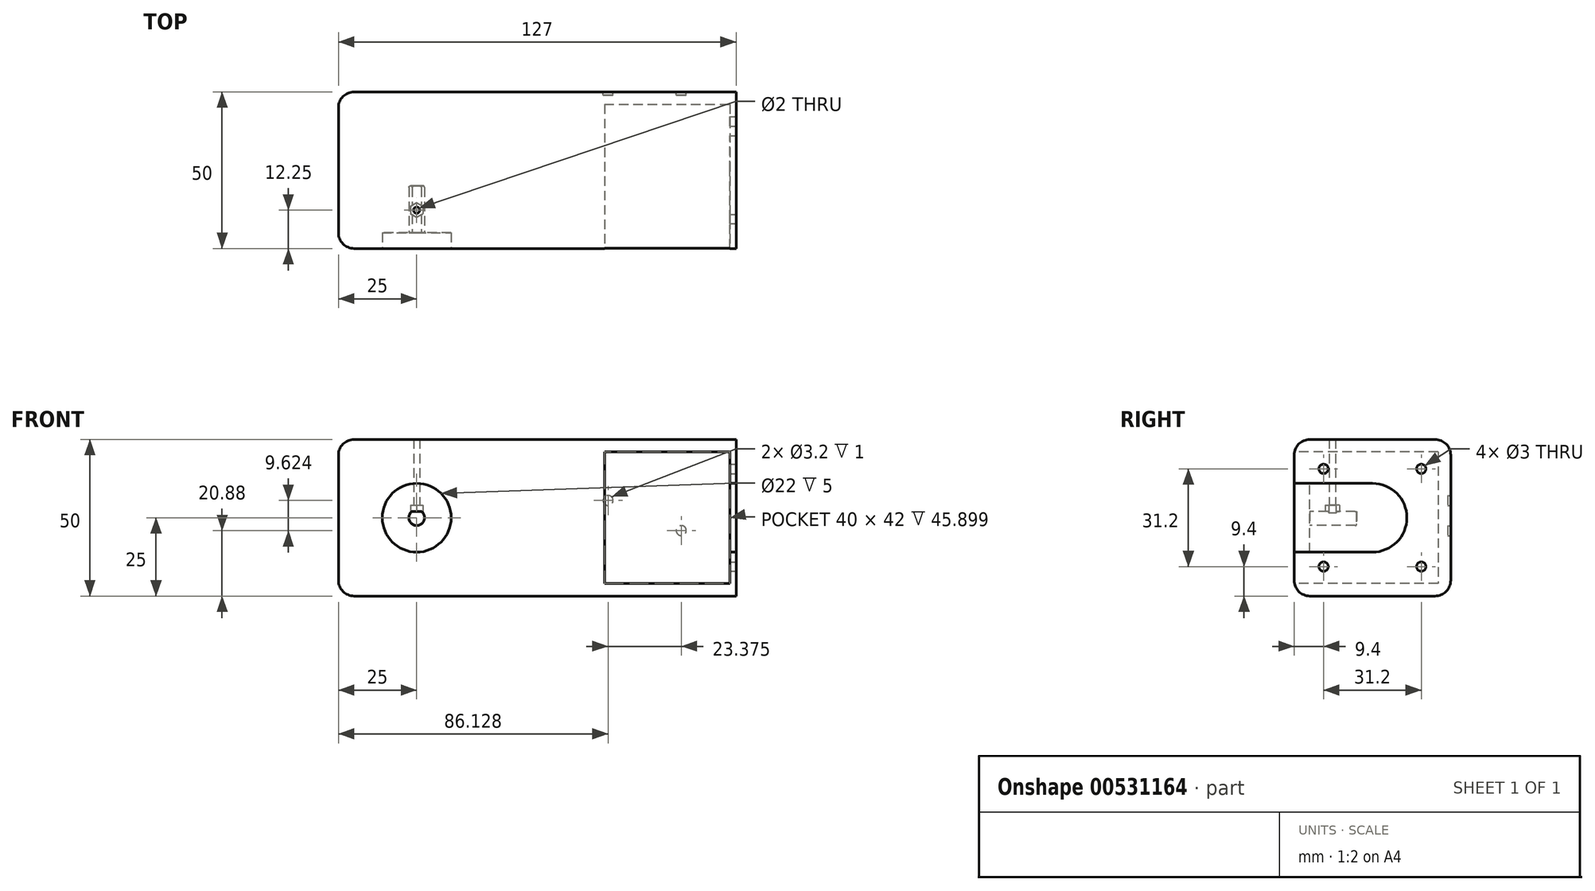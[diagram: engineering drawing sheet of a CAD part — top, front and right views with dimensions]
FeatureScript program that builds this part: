
annotation { "Feature Type Name" : "Feature", "Feature Type Description" : "" }
export const myFeature = defineFeature(function(context is Context, id is Id, definition is map)
    precondition{}
    {
        {
            var Q0;
            Q0=qCreatedBy(makeId("Front.planeOp"),FACE);
            var sketch = newSketch(context, id + "F0", { "sketchPlane" : qUnion([Q0])});
            skLineSegment(sketch, "E0.bottom", {"start": v(63.5, -25) * mm, "end": v(-63.5, -25) * mm});
            skLineSegment(sketch, "E0.top", {"start": v(63.5, 25) * mm, "end": v(-63.5, 25) * mm});
            skLineSegment(sketch, "E0.left", {"start": v(63.5, -25) * mm, "end": v(63.5, 25) * mm});
            skLineSegment(sketch, "E0.right", {"start": v(-63.5, -25) * mm, "end": v(-63.5, 25) * mm});
            skPoint(sketch, "E0.middle", {"position": v(0, 0) * mm});
            skSolve(sketch);
        }
        {
            var Q0;
            Q0 = qSketchRegion(id + "F0", true);
            extrude(context, id + "F1", {"entities" : qUnion([Q0]), "depth" : 50 * mm, "offsetDistance" : 25 * mm});
        }
        {
            var Q0;
            Q0=makeQuery(id+"F1.opExtrude","SWEPT_FACE",FACE,{"disambiguationData":[OSD([sQuery(id+"F0.wireOp",EDGE,"E0.left")])]});
            var sketch = newSketch(context, id + "F2", { "sketchPlane" : qUnion([Q0])});
            skLineSegment(sketch, "E1", {"start": v(-46, 16.76) * mm, "end": v(-41.76, 21) * mm});
            skLineSegment(sketch, "E2", {"start": v(-41.76, 21) * mm, "end": v(-8.24, 21) * mm});
            skLineSegment(sketch, "E3", {"start": v(-8.24, 21) * mm, "end": v(-4, 16.76) * mm});
            skLineSegment(sketch, "E4", {"start": v(-4, 16.76) * mm, "end": v(-4, -16.76) * mm});
            skLineSegment(sketch, "E5", {"start": v(-4, -16.76) * mm, "end": v(-8.24, -21) * mm});
            skLineSegment(sketch, "E6", {"start": v(-8.24, -21) * mm, "end": v(-41.76, -21) * mm});
            skLineSegment(sketch, "E7", {"start": v(-41.76, -21) * mm, "end": v(-46, -16.76) * mm});
            skLineSegment(sketch, "E8", {"start": v(-46, -16.76) * mm, "end": v(-46, 16.76) * mm});
            skLineSegment(sketch, "E9", {"start": v(-25, 21) * mm, "end": v(-25, 25) * mm, "construction": true});
            skLineSegment(sketch, "E10", {"start": v(-25, -21) * mm, "end": v(-25, -25) * mm, "construction": true});
            skLineSegment(sketch, "E11", {"start": v(-46, 0) * mm, "end": v(-50, 0) * mm, "construction": true});
            skLineSegment(sketch, "E12", {"start": v(0, 0) * mm, "end": v(-4, 0) * mm, "construction": true});
            skSolve(sketch);
        }
        {
            var Q0;
            Q0 = qSketchRegion(id + "F2", true);
            extrude(context, id + "F3", {"entities" : qUnion([Q0]), "operationType" : NewBodyOperationType.REMOVE, "oppositeDirection" : true, "depth" : 42 * mm, "offsetDistance" : 25 * mm});
        }
        {
            var Q0;
            Q0=makeQuery(id+"F1.opExtrude","CAP_FACE",FACE,{"disambiguationData":[OSD([sQuery(id+"F0.wireOp",EDGE,"E0.bottom"),sQuery(id+"F0.wireOp",EDGE,"E0.top"),sQuery(id+"F0.wireOp",EDGE,"E0.left"),sQuery(id+"F0.wireOp",EDGE,"E0.right")])],"isStart":false});
            var sketch = newSketch(context, id + "F4", { "sketchPlane" : qUnion([Q0])});
            skCircle(sketch, "E13", {"center": v(-38.5, 0) * mm, "radius": 11 * mm});
            skSolve(sketch);
        }
        {
            var Q0;
            Q0 = qSketchRegion(id + "F4", true);
            extrude(context, id + "F5", {"entities" : qUnion([Q0]), "operationType" : NewBodyOperationType.REMOVE, "oppositeDirection" : true, "depth" : 5 * mm, "offsetDistance" : 25 * mm});
        }
        {
            var Q0;
            Q0=makeQuery(id+"F5.boolean.opBoolean","COPY",FACE,{"derivedFrom":makeQuery(id+"F5.opExtrude","CAP_FACE",FACE,{"disambiguationData":[OSD([sQuery(id+"F4.wireOp",EDGE,"E13")])],"isStart":false})});
            var sketch = newSketch(context, id + "F6", { "sketchPlane" : qUnion([Q0])});
            skArc(sketch, "E14", {"start": v(-40, 2) * mm, "mid": v(-38.5, -2.5) * mm, "end": v(-37, 2) * mm});
            skLineSegment(sketch, "E15", {"start": v(-40, 2) * mm, "end": v(-37, 2) * mm});
            skSolve(sketch);
        }
        {
            var Q0;
            Q0 = qSketchRegion(id + "F6", true);
            extrude(context, id + "F7", {"entities" : qUnion([Q0]), "operationType" : NewBodyOperationType.REMOVE, "oppositeDirection" : true, "depth" : 15 * mm, "offsetDistance" : 25 * mm});
        }
        {
            var Q0;
            Q0=makeQuery(id+"F7.boolean.opBoolean","COPY",EDGE,{"derivedFrom":makeQuery(id+"F7.opExtrude","CAP_EDGE",EDGE,{"disambiguationData":[OSD([sQuery(id+"F6.wireOp",EDGE,"E14")])],"isStart":false})});
            fillet(context, id + "F8", {"entities" : qUnion([Q0]), "radius" : .5 * mm, "tangentPropagation" : true, "allowEdgeOverflow" : false});
        }
        {
            var Q0;
            Q0=makeQuery(id+"F1.opExtrude","CAP_EDGE",EDGE,{"disambiguationData":[OSD([sQuery(id+"F0.wireOp",EDGE,"E0.top")])],"isStart":false});
            var Q1;
            Q1=makeQuery(id+"F1.opExtrude","CAP_EDGE",EDGE,{"disambiguationData":[OSD([sQuery(id+"F0.wireOp",EDGE,"E0.bottom")])],"isStart":false});
            var Q2;
            Q2=makeQuery(id+"F1.opExtrude","CAP_EDGE",EDGE,{"disambiguationData":[OSD([sQuery(id+"F0.wireOp",EDGE,"E0.top")])],"isStart":true});
            var Q3;
            Q3=makeQuery(id+"F1.opExtrude","CAP_EDGE",EDGE,{"disambiguationData":[OSD([sQuery(id+"F0.wireOp",EDGE,"E0.bottom")])],"isStart":true});
            var Q4;
            Q4=makeQuery(id+"F1.opExtrude","SWEPT_EDGE",EDGE,{"disambiguationData":[OSD([sQuery(id+"F0.wireOp",EDGE,"E0.top"),sQuery(id+"F0.wireOp",EDGE,"E0.right")])]});
            var Q5;
            Q5=makeQuery(id+"F1.opExtrude","SWEPT_EDGE",EDGE,{"disambiguationData":[OSD([sQuery(id+"F0.wireOp",EDGE,"E0.bottom"),sQuery(id+"F0.wireOp",EDGE,"E0.right")])]});
            var Q6;
            Q6=makeQuery(id+"F1.opExtrude","CAP_EDGE",EDGE,{"disambiguationData":[OSD([sQuery(id+"F0.wireOp",EDGE,"E0.right")])],"isStart":true});
            var Q7;
            Q7=makeQuery(id+"F1.opExtrude","CAP_EDGE",EDGE,{"disambiguationData":[OSD([sQuery(id+"F0.wireOp",EDGE,"E0.right")])],"isStart":false});
            fillet(context, id + "F9", {"entities" : qUnion([Q0, Q1, Q2, Q3, Q4, Q5, Q6, Q7]), "radius" : 5 * mm, "tangentPropagation" : true, "allowEdgeOverflow" : false});
        }
        {
            var Q0;
            Q0=makeQuery(id+"F1.opExtrude","SWEPT_FACE",FACE,{"disambiguationData":[OSD([sQuery(id+"F0.wireOp",EDGE,"E0.left")])]});
            var sketch = newSketch(context, id + "F10", { "sketchPlane" : qUnion([Q0])});
            skPoint(sketch, "E16.middle", {"position": v(-25, 0) * mm});
            skLineSegment(sketch, "E17", {"start": v(-46, -16.76) * mm, "end": v(-41.76, -21) * mm});
            skLineSegment(sketch, "E18", {"start": v(-46, -16.76) * mm, "end": v(-46, 16.76) * mm});
            skLineSegment(sketch, "E19", {"start": v(-46, 16.76) * mm, "end": v(-41.76, 21) * mm});
            skLineSegment(sketch, "E20", {"start": v(-41.76, -21) * mm, "end": v(-8.24, -21) * mm});
            skLineSegment(sketch, "E21", {"start": v(-8.24, -21) * mm, "end": v(-4, -16.76) * mm});
            skLineSegment(sketch, "E22", {"start": v(-4, -16.76) * mm, "end": v(-4, 16.76) * mm});
            skLineSegment(sketch, "E23", {"start": v(-4, 16.76) * mm, "end": v(-8.24, 21) * mm});
            skLineSegment(sketch, "E24", {"start": v(-8.24, 21) * mm, "end": v(-41.76, 21) * mm});
            skLineSegment(sketch, "E25", {"start": v(-25, 0) * mm, "end": v(-4, 0) * mm, "construction": true});
            skLineSegment(sketch, "E26", {"start": v(-25, 0) * mm, "end": v(-25, 21) * mm, "construction": true});
            skLineSegment(sketch, "E27", {"start": v(-25, 0) * mm, "end": v(-25, -21) * mm, "construction": true});
            skLineSegment(sketch, "E28", {"start": v(-25, 0) * mm, "end": v(-46, 0) * mm, "construction": true});
            skLineSegment(sketch, "E29.bottom", {"start": v(-9.4, -15.6) * mm, "end": v(-40.6, -15.6) * mm});
            skLineSegment(sketch, "E29.top", {"start": v(-9.4, 15.6) * mm, "end": v(-40.6, 15.6) * mm});
            skLineSegment(sketch, "E29.left", {"start": v(-9.4, -15.6) * mm, "end": v(-9.4, 15.6) * mm});
            skLineSegment(sketch, "E29.right", {"start": v(-40.6, -15.6) * mm, "end": v(-40.6, 15.6) * mm});
            skCircle(sketch, "E30", {"center": v(-40.6, 15.6) * mm, "radius": 1.5 * mm});
            skCircle(sketch, "E31", {"center": v(-9.4, 15.6) * mm, "radius": 1.5 * mm});
            skCircle(sketch, "E32", {"center": v(-9.4, -15.6) * mm, "radius": 1.5 * mm});
            skCircle(sketch, "E33", {"center": v(-40.6, -15.6) * mm, "radius": 1.5 * mm});
            skLineSegment(sketch, "E34.bottom", {"start": v(-33.1, 21) * mm, "end": v(-16.9, 21) * mm});
            skLineSegment(sketch, "E35", {"start": v(-16.9, 21) * mm, "end": v(-8.24, 21) * mm, "construction": true});
            skLineSegment(sketch, "E36", {"start": v(-33.1, 21) * mm, "end": v(-41.76, 21) * mm, "construction": true});
            skSolve(sketch);
        }
        {
            var Q0;
            Q0=makeQuery(id+"FMPlXjMWnGon0a9_1.boolean.opBoolean","MERGE",FACE,{"derivedFrom":[makeQuery(id+"F1.opExtrude","SWEPT_FACE",FACE,{"disambiguationData":[OSD([sQuery(id+"F0.wireOp",EDGE,"E0.left")])]}),makeQuery(id+"FMPlXjMWnGon0a9_1.opExtrude","CAP_FACE",FACE,{"disambiguationData":[OSD([sQuery(id+"F10.wireOp",EDGE,"7e317716-1d10-45a1-bd77-1f030e6113fa"),sQuery(id+"F10.wireOp",EDGE,"a9baf04a-07a7-4197-b8e6-3b8d32bb72bb"),sQuery(id+"F10.wireOp",EDGE,"0afc13e5-a02a-4f5f-93d0-e888419d06cc"),sQuery(id+"F10.wireOp",EDGE,"3bec6db8-7ce1-4d02-bc73-26e9fa90f9ca"),sQuery(id+"F10.wireOp",EDGE,"4aacd247-3ff8-4e3c-a909-91dfdb2c83a4"),sQuery(id+"F10.wireOp",EDGE,"cb9adce3-904a-4ef7-b8bb-e01b4716a234"),sQuery(id+"F10.wireOp",EDGE,"422983aa-e8dd-4766-8909-e12d55b331f8"),sQuery(id+"F10.wireOp",EDGE,"0b41c461-bc85-4d50-8d82-77dba81586c2"),sQuery(id+"F10.wireOp",EDGE,"d2e1f196-5fb4-45e0-a0eb-1cf5d613c0ba"),sQuery(id+"F10.wireOp",EDGE,"4a6b8d65-2de6-42a6-bc2a-ce8d35ed1551"),sQuery(id+"F10.wireOp",EDGE,"09a8e3e9-80f5-4af3-9dc7-d9ba060c69f5"),sQuery(id+"F10.wireOp",EDGE,"eed8e5a7-c47a-4f85-b74d-ca0ec0753e29"),sQuery(id+"F10.wireOp",EDGE,"10ccaaaf-dc0f-476e-ab06-8ddfde2fb4c6")])],"isStart":true})]});
            var sketch = newSketch(context, id + "F11", { "sketchPlane" : qUnion([Q0])});
            skLineSegment(sketch, "E37", {"start": v(-25, -11) * mm, "end": v(-50, -11) * mm});
            skLineSegment(sketch, "E38", {"start": v(-25, 11) * mm, "end": v(-50, 11) * mm});
            skArc(sketch, "E39", {"start": v(-25, -11) * mm, "mid": v(-14, 0) * mm, "end": v(-25, 11) * mm});
            skLineSegment(sketch, "E40", {"start": v(-50, 11) * mm, "end": v(-50, -11) * mm});
            skSolve(sketch);
        }
        {
            var Q0;
            Q0=makeQuery(id+"F1.opExtrude","CAP_FACE",FACE,{"disambiguationData":[OSD([sQuery(id+"F0.wireOp",EDGE,"E0.bottom"),sQuery(id+"F0.wireOp",EDGE,"E0.top"),sQuery(id+"F0.wireOp",EDGE,"E0.left"),sQuery(id+"F0.wireOp",EDGE,"E0.right")])],"isStart":false});
            var sketch = newSketch(context, id + "F12", { "sketchPlane" : qUnion([Q0])});
            skLineSegment(sketch, "E41.bottom", {"start": v(21.5, 21) * mm, "end": v(61.5, 21) * mm});
            skLineSegment(sketch, "E41.top", {"start": v(21.5, -21) * mm, "end": v(61.5, -21) * mm});
            skLineSegment(sketch, "E41.left", {"start": v(21.5, 21) * mm, "end": v(21.5, -21) * mm});
            skLineSegment(sketch, "E41.right", {"start": v(61.5, 21) * mm, "end": v(61.5, -21) * mm});
            skLineSegment(sketch, "E42", {"start": v(61.5, 21) * mm, "end": v(61.5, 25) * mm, "construction": true});
            skLineSegment(sketch, "E43", {"start": v(63.5, -21) * mm, "end": v(63.5, -25) * mm, "construction": true});
            skSolve(sketch);
        }
        {
            var Q0;
            Q0 = qSketchRegion(id + "F12", true);
            extrude(context, id + "F13", {"entities" : qUnion([Q0]), "operationType" : NewBodyOperationType.REMOVE, "oppositeDirection" : true, "depth" : 46 * mm, "offsetDistance" : 25 * mm});
        }
        {
            var Q0;
            Q0=makeQuery(id+"F1.opExtrude","CAP_FACE",FACE,{"disambiguationData":[OSD([sQuery(id+"F0.wireOp",EDGE,"E0.bottom"),sQuery(id+"F0.wireOp",EDGE,"E0.top"),sQuery(id+"F0.wireOp",EDGE,"E0.left"),sQuery(id+"F0.wireOp",EDGE,"E0.right")])],"isStart":true});
            var sketch = newSketch(context, id + "F14", { "sketchPlane" : qUnion([Q0])});
            skCircle(sketch, "E44", {"center": v(-22.63, 5.5) * mm, "radius": 1.6 * mm});
            skCircle(sketch, "E45", {"center": v(-46, -4.12) * mm, "radius": 1.6 * mm});
            skLineSegment(sketch, "E46.left", {"start": v(-22.5, 8) * mm, "end": v(-45.33, 9.15) * mm});
            skLineSegment(sketch, "E46.right", {"start": v(-23.3, -7.77) * mm, "end": v(-46.13, -6.62) * mm});
            skLineSegment(sketch, "E47", {"start": v(-20.13, 5.38) * mm, "end": v(-20.68, -5.4) * mm});
            skLineSegment(sketch, "E48", {"start": v(-47.96, 6.78) * mm, "end": v(-48.5, -4) * mm});
            skArc(sketch, "E49", {"start": v(-20.13, 5.38) * mm, "mid": v(-20.77, 7.18) * mm, "end": v(-22.5, 8) * mm});
            skArc(sketch, "E50", {"start": v(-23.3, -7.77) * mm, "mid": v(-21.5, -7.13) * mm, "end": v(-20.68, -5.4) * mm});
            skArc(sketch, "E51", {"start": v(-45.33, 9.15) * mm, "mid": v(-47.14, 8.51) * mm, "end": v(-47.96, 6.78) * mm});
            skArc(sketch, "E52", {"start": v(-48.5, -4) * mm, "mid": v(-47.86, -5.8) * mm, "end": v(-46.13, -6.62) * mm});
            skSolve(sketch);
        }
        {
            var Q0;
            Q0=makeQuery(id+"F14.imprint","IMPRINT",FACE,{"disambiguationData":[TD([[makeQuery(id+"F14.imprint","IMPRINT",EDGE,{"derivedFrom":sQuery(id+"F14.wireOp",EDGE,"E45")}),1.0]])]});
            var Q1;
            Q1=makeQuery(id+"F14.imprint","IMPRINT",FACE,{"disambiguationData":[TD([[makeQuery(id+"F14.imprint","IMPRINT",EDGE,{"derivedFrom":sQuery(id+"F14.wireOp",EDGE,"E44")}),1.0]])]});
            extrude(context, id + "F15", {"entities" : qUnion([Q0, Q1]), "operationType" : NewBodyOperationType.REMOVE, "oppositeDirection" : true, "depth" : 1 * mm, "offsetDistance" : 25 * mm});
        }
        {
            var Q0;
            Q0=makeQuery(id+"F7.boolean.opBoolean","COPY",FACE,{"derivedFrom":makeQuery(id+"F7.opExtrude","SWEPT_FACE",FACE,{"disambiguationData":[OSD([sQuery(id+"F6.wireOp",EDGE,"E15")])]})});
            var sketch = newSketch(context, id + "F16", { "sketchPlane" : qUnion([Q0])});
            skCircle(sketch, "E53", {"center": v(-38.5, 37.75) * mm, "radius": 1 * mm});
            skLineSegment(sketch, "E54", {"start": v(-38.5, 45) * mm, "end": v(-38.5, 30.5) * mm, "construction": true});
            skCircle(sketch, "E55.cCircle", {"center": v(-38.5, 37.75) * mm, "radius": 2 * mm, "construction": true});
            skLineSegment(sketch, "E55.0", {"start": v(-38.5, 40.06) * mm, "end": v(-36.5, 38.9) * mm});
            skLineSegment(sketch, "E55.1", {"start": v(-36.5, 38.9) * mm, "end": v(-36.5, 36.6) * mm});
            skLineSegment(sketch, "E55.2", {"start": v(-36.5, 36.6) * mm, "end": v(-38.5, 35.44) * mm});
            skLineSegment(sketch, "E55.3", {"start": v(-38.5, 35.44) * mm, "end": v(-40.5, 36.6) * mm});
            skLineSegment(sketch, "E55.4", {"start": v(-40.5, 36.6) * mm, "end": v(-40.5, 38.9) * mm});
            skLineSegment(sketch, "E55.5", {"start": v(-40.5, 38.9) * mm, "end": v(-38.5, 40.06) * mm});
            skPoint(sketch, "E55.0.midPoint", {"position": v(-37.5, 39.48) * mm});
            skSolve(sketch);
        }
        {
            var Q0;
            Q0 = qSketchRegion(id + "F16", true);
            extrude(context, id + "F17", {"entities" : qUnion([Q0]), "operationType" : NewBodyOperationType.REMOVE, "oppositeDirection" : true, "depth" : 2 * mm, "offsetDistance" : 25 * mm, "hasSecondDirection" : true, "secondDirectionOppositeDirection" : false, "secondDirectionDepth" : 1.03 * mm});
        }
        {
            var Q0;
            Q0=makeQuery(id+"F17.boolean.opBoolean","SPLIT",FACE,{"disambiguationData":[TD([makeQuery(id+"F17.opExtrude","SWEPT_FACE",FACE,{"disambiguationData":[OSD([sQuery(id+"F16.wireOp",EDGE,"E53")])]})])],"derivedFrom":makeQuery(id+"F7.boolean.opBoolean","COPY",FACE,{"derivedFrom":makeQuery(id+"F7.opExtrude","SWEPT_FACE",FACE,{"disambiguationData":[OSD([sQuery(id+"F6.wireOp",EDGE,"E15")])]})})});
            extrude(context, id + "F18", {"entities" : qUnion([Q0]), "operationType" : NewBodyOperationType.REMOVE, "oppositeDirection" : true, "depth" : 25 * mm, "offsetDistance" : 25 * mm});
        }
        {
            var Q0;
            Q0=makeQuery(id+"F10.imprint","IMPRINT",FACE,{"disambiguationData":[TD([[makeQuery(id+"F10.imprint","IMPRINT",EDGE,{"derivedFrom":sQuery(id+"F10.wireOp",EDGE,"E17")}),-1.0]])]});
            var Q1;
            {var subQ5=sQuery(id+"F10.wireOp",EDGE,"E32");var subQ10=sQuery(id+"F10.wireOp",EDGE,"E29.bottom");var subQ15=makeQuery(id+"F10.imprint","INTERSECT",VERTEX,{"derivedFrom":[subQ10,subQ5]});Q1=makeQuery(id+"F10.imprint","IMPRINT",FACE,{"disambiguationData":[TD([[makeQuery(id+"F10.imprint","IMPRINT",EDGE,{"disambiguationData":[TD([[subQ15,-1.0]])],"derivedFrom":subQ10}),-1.0]])]});}
            extrude(context, id + "F19", {"entities" : qUnion([Q0, Q1]), "operationType" : NewBodyOperationType.ADD, "oppositeDirection" : true, "depth" : 2 * mm, "offsetDistance" : 25 * mm});
        }
        {
            var Q0;
            {var subQ0=sQuery(id+"F11.wireOp",EDGE,"E39");Q0=makeQuery(id+"F11.imprint","IMPRINT",FACE,{"disambiguationData":[TD([[makeQuery(id+"F11.imprint","IMPRINT",EDGE,{"derivedFrom":subQ0}),1.0]])]});}
            var Q1;
            {var subQ0=sQuery(id+"F11.wireOp",EDGE,"E40");Q1=makeQuery(id+"F11.imprint","IMPRINT",FACE,{"disambiguationData":[TD([[makeQuery(id+"F11.imprint","IMPRINT",EDGE,{"derivedFrom":subQ0}),-1.0]])]});}
            extrude(context, id + "F20", {"entities" : qUnion([Q0, Q1]), "operationType" : NewBodyOperationType.REMOVE, "oppositeDirection" : true, "depth" : 25 * mm, "offsetDistance" : 25 * mm});
        }
    });
